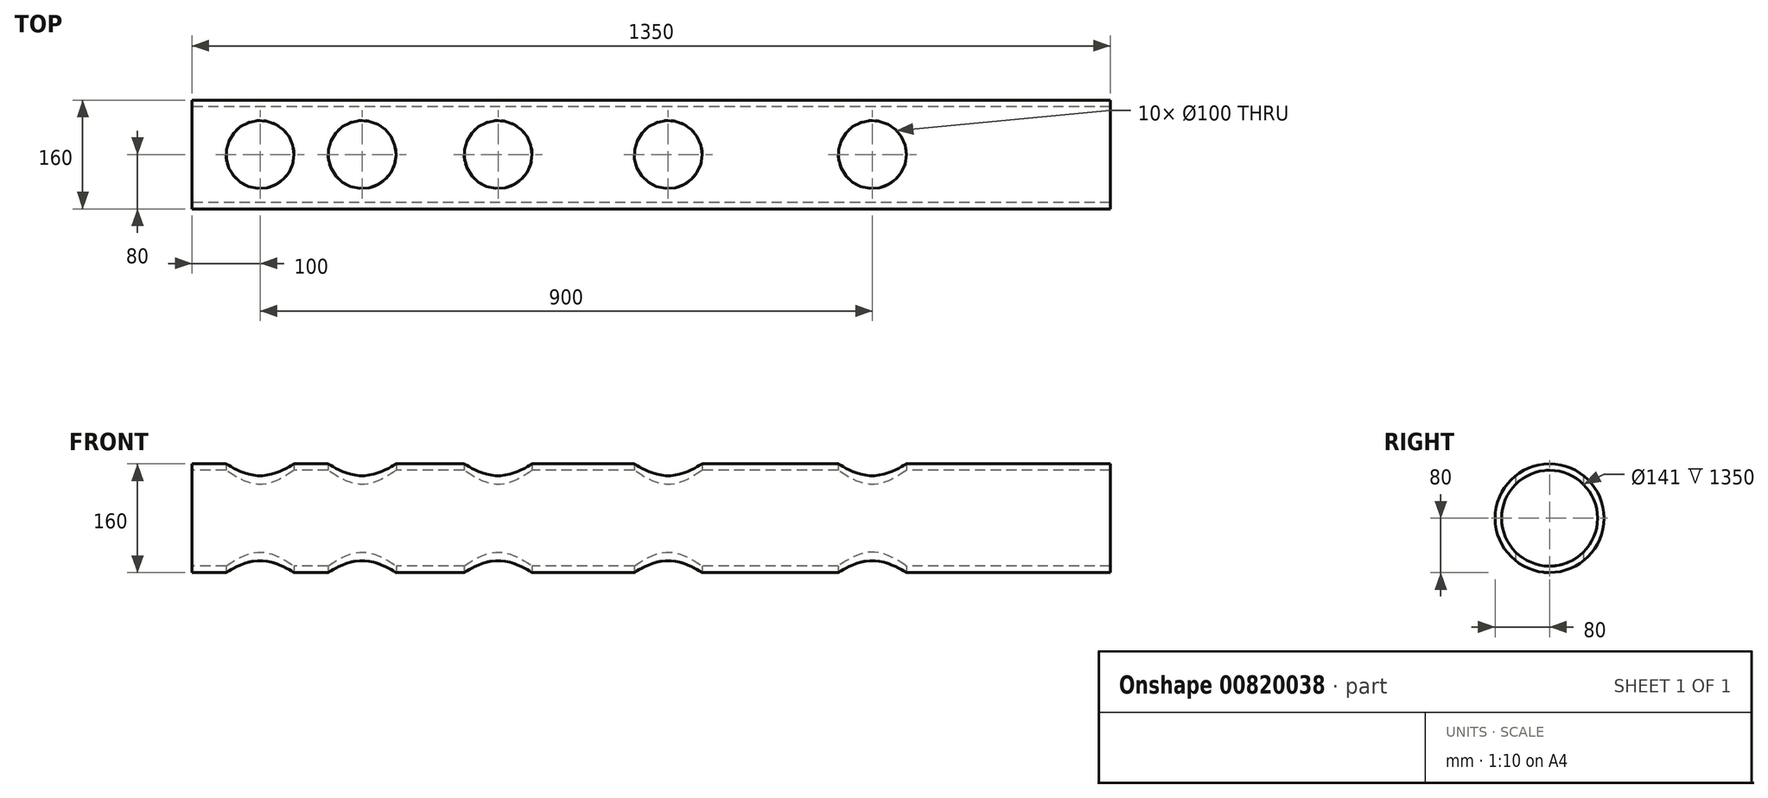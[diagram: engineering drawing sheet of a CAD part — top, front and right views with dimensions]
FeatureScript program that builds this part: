
annotation { "Feature Type Name" : "Feature", "Feature Type Description" : "" }
export const myFeature = defineFeature(function(context is Context, id is Id, definition is map)
    precondition{}
    {
        {
            var Q0;
            Q0=qCreatedBy(makeId("Right.planeOp"),FACE);
            var sketch = newSketch(context, id + "F0", { "sketchPlane" : qUnion([Q0])});
            skCircle(sketch, "E0", {"center": v(0, 0) * mm, "radius": 80 * mm});
            skCircle(sketch, "E1", {"center": v(0, 0) * mm, "radius": 70.5 * mm});
            skSolve(sketch);
        }
        {
            var Q0;
            Q0=qSketchRegion(id+"F0",true);
            extrude(context, id + "F1", {"entities" : qUnion([Q0]), "depth" : 1350 * mm, "offsetDistance" : 25 * mm});
        }
        {
            var Q0;
            Q0=qCreatedBy(makeId("Top.planeOp"),FACE);
            var sketch = newSketch(context, id + "F2", { "sketchPlane" : qUnion([Q0])});
            skLineSegment(sketch, "E2", {"start": v(0, 0) * mm, "end": v(1100, 0) * mm});
            skLineSegment(sketch, "E3", {"start": v(1100, 0) * mm, "end": v(1151.8, -193.18) * mm});
            skLineSegment(sketch, "E4", {"start": v(0, 0) * mm, "end": v(100, 0) * mm});
            skCircle(sketch, "E5", {"center": v(100, 0) * mm, "radius": 50 * mm});
            skLineSegment(sketch, "E6", {"start": v(100, 0) * mm, "end": v(250, 0) * mm});
            skLineSegment(sketch, "E7", {"start": v(250, 0) * mm, "end": v(450, 0) * mm});
            skLineSegment(sketch, "E8", {"start": v(450, 0) * mm, "end": v(700, 0) * mm});
            skLineSegment(sketch, "E9", {"start": v(700, 0) * mm, "end": v(1000, 0) * mm});
            skCircle(sketch, "E10", {"center": v(250, 0) * mm, "radius": 50 * mm});
            skCircle(sketch, "E11", {"center": v(450, 0) * mm, "radius": 50 * mm});
            skCircle(sketch, "E12", {"center": v(700, 0) * mm, "radius": 50 * mm});
            skCircle(sketch, "E13", {"center": v(1000, 0) * mm, "radius": 50 * mm});
            skPoint(sketch, "E14.middle", {"position": v(0, 0) * mm});
            skLineSegment(sketch, "E15", {"start": v(0, 0) * mm, "end": v(0, 130) * mm});
            skLineSegment(sketch, "E16", {"start": v(0, 0) * mm, "end": v(0, -130) * mm});
            skPoint(sketch, "E17.orphan", {"position": v(75, -130) * mm});
            skPoint(sketch, "E18.orphan", {"position": v(75, 130) * mm});
            skArc(sketch, "E19", {"start": v(-35.75, 130) * mm, "mid": v(-50, 0) * mm, "end": v(-35.75, -130) * mm});
            skLineSegment(sketch, "E20", {"start": v(-35.75, 130) * mm, "end": v(0, 130) * mm});
            skLineSegment(sketch, "E21", {"start": v(0, -130) * mm, "end": v(-35.75, -130) * mm});
            skSolve(sketch);
        }
        {
            var Q0;
            {var subQ0=sQuery(id+"F2.wireOp",EDGE,"E6");var subQ1=sQuery(id+"F2.wireOp",EDGE,"E4");var subQ2=makeQuery(id+"F2.imprint","INTERSECT",VERTEX,{"derivedFrom":[subQ1,subQ0]});Q0=makeQuery(id+"F2.imprint","IMPRINT",FACE,{"disambiguationData":[TD([[makeQuery(id+"F2.imprint","IMPRINT",EDGE,{"disambiguationData":[TD([[subQ2,1.0]])],"derivedFrom":subQ1}),-1.0]])]});}
            var Q1;
            {var subQ0=sQuery(id+"F2.wireOp",EDGE,"E6");var subQ1=sQuery(id+"F2.wireOp",EDGE,"E4");var subQ2=makeQuery(id+"F2.imprint","INTERSECT",VERTEX,{"derivedFrom":[subQ1,subQ0]});Q1=makeQuery(id+"F2.imprint","IMPRINT",FACE,{"disambiguationData":[TD([[makeQuery(id+"F2.imprint","IMPRINT",EDGE,{"disambiguationData":[TD([[subQ2,1.0]])],"derivedFrom":subQ1}),1.0]])]});}
            var Q2;
            {var subQ0=sQuery(id+"F2.wireOp",EDGE,"E7");var subQ1=sQuery(id+"F2.wireOp",EDGE,"E6");var subQ2=makeQuery(id+"F2.imprint","INTERSECT",VERTEX,{"derivedFrom":[subQ1,subQ0]});Q2=makeQuery(id+"F2.imprint","IMPRINT",FACE,{"disambiguationData":[TD([[makeQuery(id+"F2.imprint","IMPRINT",EDGE,{"disambiguationData":[TD([[subQ2,1.0]])],"derivedFrom":subQ1}),1.0]])]});}
            var Q3;
            {var subQ0=sQuery(id+"F2.wireOp",EDGE,"E7");var subQ1=sQuery(id+"F2.wireOp",EDGE,"E6");var subQ2=makeQuery(id+"F2.imprint","INTERSECT",VERTEX,{"derivedFrom":[subQ1,subQ0]});Q3=makeQuery(id+"F2.imprint","IMPRINT",FACE,{"disambiguationData":[TD([[makeQuery(id+"F2.imprint","IMPRINT",EDGE,{"disambiguationData":[TD([[subQ2,1.0]])],"derivedFrom":subQ1}),-1.0]])]});}
            var Q4;
            {var subQ0=sQuery(id+"F2.wireOp",EDGE,"E8");var subQ1=sQuery(id+"F2.wireOp",EDGE,"E7");var subQ2=makeQuery(id+"F2.imprint","INTERSECT",VERTEX,{"derivedFrom":[subQ1,subQ0]});Q4=makeQuery(id+"F2.imprint","IMPRINT",FACE,{"disambiguationData":[TD([[makeQuery(id+"F2.imprint","IMPRINT",EDGE,{"disambiguationData":[TD([[subQ2,1.0]])],"derivedFrom":subQ1}),1.0]])]});}
            var Q5;
            {var subQ0=sQuery(id+"F2.wireOp",EDGE,"E8");var subQ1=sQuery(id+"F2.wireOp",EDGE,"E7");var subQ2=makeQuery(id+"F2.imprint","INTERSECT",VERTEX,{"derivedFrom":[subQ1,subQ0]});Q5=makeQuery(id+"F2.imprint","IMPRINT",FACE,{"disambiguationData":[TD([[makeQuery(id+"F2.imprint","IMPRINT",EDGE,{"disambiguationData":[TD([[subQ2,1.0]])],"derivedFrom":subQ1}),-1.0]])]});}
            var Q6;
            {var subQ0=sQuery(id+"F2.wireOp",EDGE,"E9");var subQ1=sQuery(id+"F2.wireOp",EDGE,"E8");var subQ2=makeQuery(id+"F2.imprint","INTERSECT",VERTEX,{"derivedFrom":[subQ1,subQ0]});Q6=makeQuery(id+"F2.imprint","IMPRINT",FACE,{"disambiguationData":[TD([[makeQuery(id+"F2.imprint","IMPRINT",EDGE,{"disambiguationData":[TD([[subQ2,1.0]])],"derivedFrom":subQ1}),1.0]])]});}
            var Q7;
            {var subQ0=sQuery(id+"F2.wireOp",EDGE,"E9");var subQ1=sQuery(id+"F2.wireOp",EDGE,"E8");var subQ2=makeQuery(id+"F2.imprint","INTERSECT",VERTEX,{"derivedFrom":[subQ1,subQ0]});Q7=makeQuery(id+"F2.imprint","IMPRINT",FACE,{"disambiguationData":[TD([[makeQuery(id+"F2.imprint","IMPRINT",EDGE,{"disambiguationData":[TD([[subQ2,1.0]])],"derivedFrom":subQ1}),-1.0]])]});}
            var Q8;
            {var subQ0=sQuery(id+"F2.wireOp",EDGE,"E9");var subQ1=sQuery(id+"F2.wireOp",EDGE,"E2");var subQ2=makeQuery(id+"F2.imprint","INTERSECT",VERTEX,{"derivedFrom":[subQ1,subQ0]});Q8=makeQuery(id+"F2.imprint","IMPRINT",FACE,{"disambiguationData":[TD([[makeQuery(id+"F2.imprint","IMPRINT",EDGE,{"disambiguationData":[TD([[subQ2,-1.0]])],"derivedFrom":subQ1}),1.0]])]});}
            var Q9;
            {var subQ0=sQuery(id+"F2.wireOp",EDGE,"E9");var subQ1=sQuery(id+"F2.wireOp",EDGE,"E2");var subQ2=makeQuery(id+"F2.imprint","INTERSECT",VERTEX,{"derivedFrom":[subQ1,subQ0]});Q9=makeQuery(id+"F2.imprint","IMPRINT",FACE,{"disambiguationData":[TD([[makeQuery(id+"F2.imprint","IMPRINT",EDGE,{"disambiguationData":[TD([[subQ2,-1.0]])],"derivedFrom":subQ1}),-1.0]])]});}
            extrude(context, id + "F3", {"entities" : qUnion([Q0, Q1, Q2, Q3, Q4, Q5, Q6, Q7, Q8, Q9]), "operationType" : NewBodyOperationType.REMOVE, "endBound" : BoundingType.SYMMETRIC, "depth" : 200 * mm, "offsetDistance" : 25 * mm});
        }
    });
